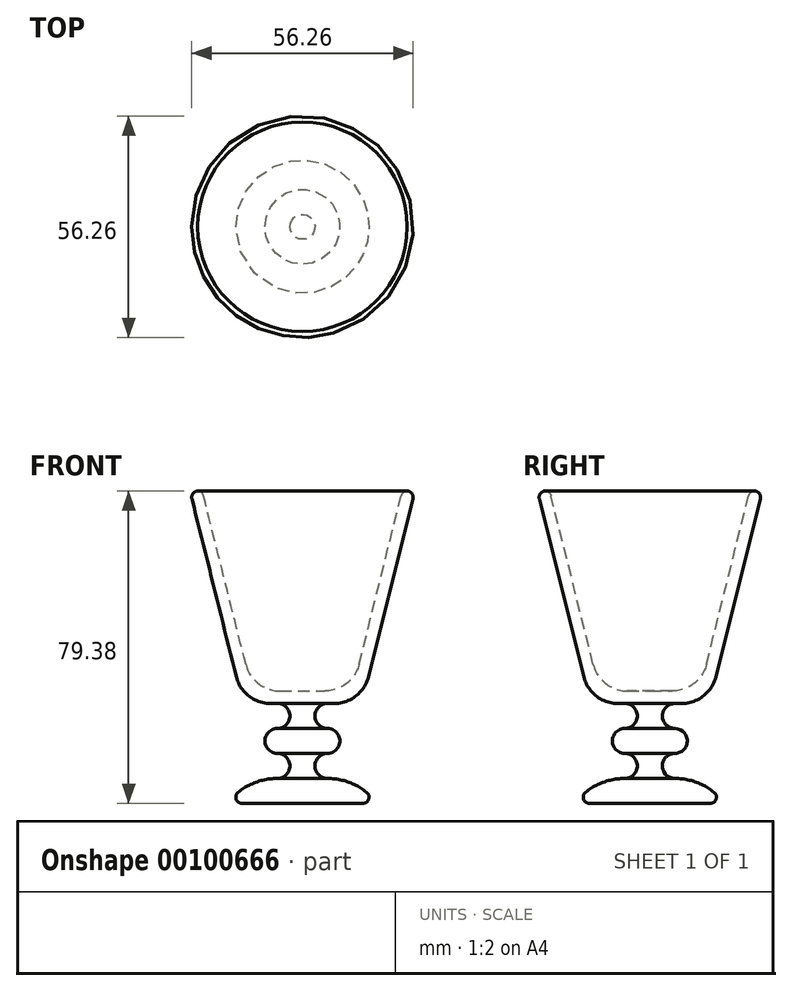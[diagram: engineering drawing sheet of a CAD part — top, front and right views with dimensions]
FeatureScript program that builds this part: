
annotation { "Feature Type Name" : "Feature", "Feature Type Description" : "" }
export const myFeature = defineFeature(function(context is Context, id is Id, definition is map)
    precondition{}
    {
        {
            var Q0;
            Q0=qCreatedBy(makeId("Front.planeOp"),FACE);
            var sketch = newSketch(context, id + "F0", { "sketchPlane" : qUnion([Q0])});
            skLineSegment(sketch, "E0", {"start": v(0, 0) * mm, "end": v(-5.76, 0) * mm});
            skLineSegment(sketch, "E1", {"start": v(-14.38, 6.73) * mm, "end": v(-25.1, 49.6) * mm});
            skLineSegment(sketch, "E2", {"start": v(-26.54, 50.8) * mm, "end": v(-26.64, 50.8) * mm});
            skLineSegment(sketch, "E3", {"start": v(-28.08, 48.83) * mm, "end": v(-16.76, 3.56) * mm});
            skLineSegment(sketch, "E4", {"start": v(-8.14, -3.18) * mm, "end": v(-6.35, -3.18) * mm});
            skArc(sketch, "E5", {"start": v(-6.35, -3.18) * mm, "mid": v(-3.17, -6.35) * mm, "end": v(-6.35, -9.53) * mm});
            skArc(sketch, "E6", {"start": v(-6.35, -9.52) * mm, "mid": v(-9.52, -12.7) * mm, "end": v(-6.35, -15.88) * mm});
            skArc(sketch, "E7", {"start": v(-6.35, -15.87) * mm, "mid": v(-3.18, -19.05) * mm, "end": v(-6.35, -22.22) * mm});
            skArc(sketch, "E8", {"start": v(-6.35, -22.22) * mm, "mid": v(-11.64, -23.13) * mm, "end": v(-16.33, -25.75) * mm});
            skLineSegment(sketch, "E9", {"start": v(-15.33, -28.57) * mm, "end": v(0, -28.57) * mm});
            skPoint(sketch, "E10.visualSharp", {"position": v(-15.08, -3.18) * mm});
            skArc(sketch, "E10.filletArc", {"start": v(-16.76, 3.56) * mm, "mid": v(-13.61, -1.3) * mm, "end": v(-8.14, -3.18) * mm});
            skPoint(sketch, "E11.visualSharp", {"position": v(-12.7, 0) * mm});
            skArc(sketch, "E11.filletArc", {"start": v(-14.38, 6.73) * mm, "mid": v(-11.23, 1.88) * mm, "end": v(-5.76, 0) * mm});
            skPoint(sketch, "E12.visualSharp", {"position": v(-25.4, 50.8) * mm});
            skArc(sketch, "E12.filletArc", {"start": v(-25.1, 49.6) * mm, "mid": v(-25.66, 50.46) * mm, "end": v(-26.64, 50.8) * mm});
            skPoint(sketch, "E13.visualSharp", {"position": v(-28.58, 50.8) * mm});
            skArc(sketch, "E13.filletArc", {"start": v(-26.54, 50.8) * mm, "mid": v(-27.8, 50.19) * mm, "end": v(-28.08, 48.83) * mm});
            skPoint(sketch, "E14.visualSharp", {"position": v(-19.05, -28.57) * mm});
            skArc(sketch, "E14.filletArc", {"start": v(-16.33, -25.75) * mm, "mid": v(-16.83, -27.52) * mm, "end": v(-15.33, -28.58) * mm});
            skLineSegment(sketch, "E15", {"start": v(0, -28.57) * mm, "end": v(0, 0) * mm, "construction": true});
            skLineSegment(sketch, "E16", {"start": v(0, -28.57) * mm, "end": v(0, 0) * mm});
            skLineSegment(sketch, "E17", {"start": v(0, 0) * mm, "end": v(0, 23.9) * mm});
            skSolve(sketch);
        }
        {
            var Q0;
            Q0=makeQuery(id+"F0.imprint","IMPRINT",FACE,{"disambiguationData":[TD([[makeQuery(id+"F0.imprint","IMPRINT",EDGE,{"derivedFrom":sQuery(id+"F0.wireOp",EDGE,"E0")}),1.0]])]});
            var Q1;
            Q1=sQuery(id+"F0.wireOp",EDGE,"E17");
            revolve(context, id + "F1", {"entities" : qUnion([Q0]), "axis" : qUnion([Q1]), "revolveType" : RevolveType.FULL});
        }
        {
            var Q0;
            Q0=sQuery(id+"F0.wireOp",EDGE,"E3");
            cPlane(context, id + "F2", {"entities" : qUnion([Q0]), "cplaneType" : CPlaneType.LINE_ANGLE, "offset" : 152.4 * mm, "angle" : 0 * degree, "width" : 152.4 * mm, "height" : 152.4 * mm});
        }
    });
